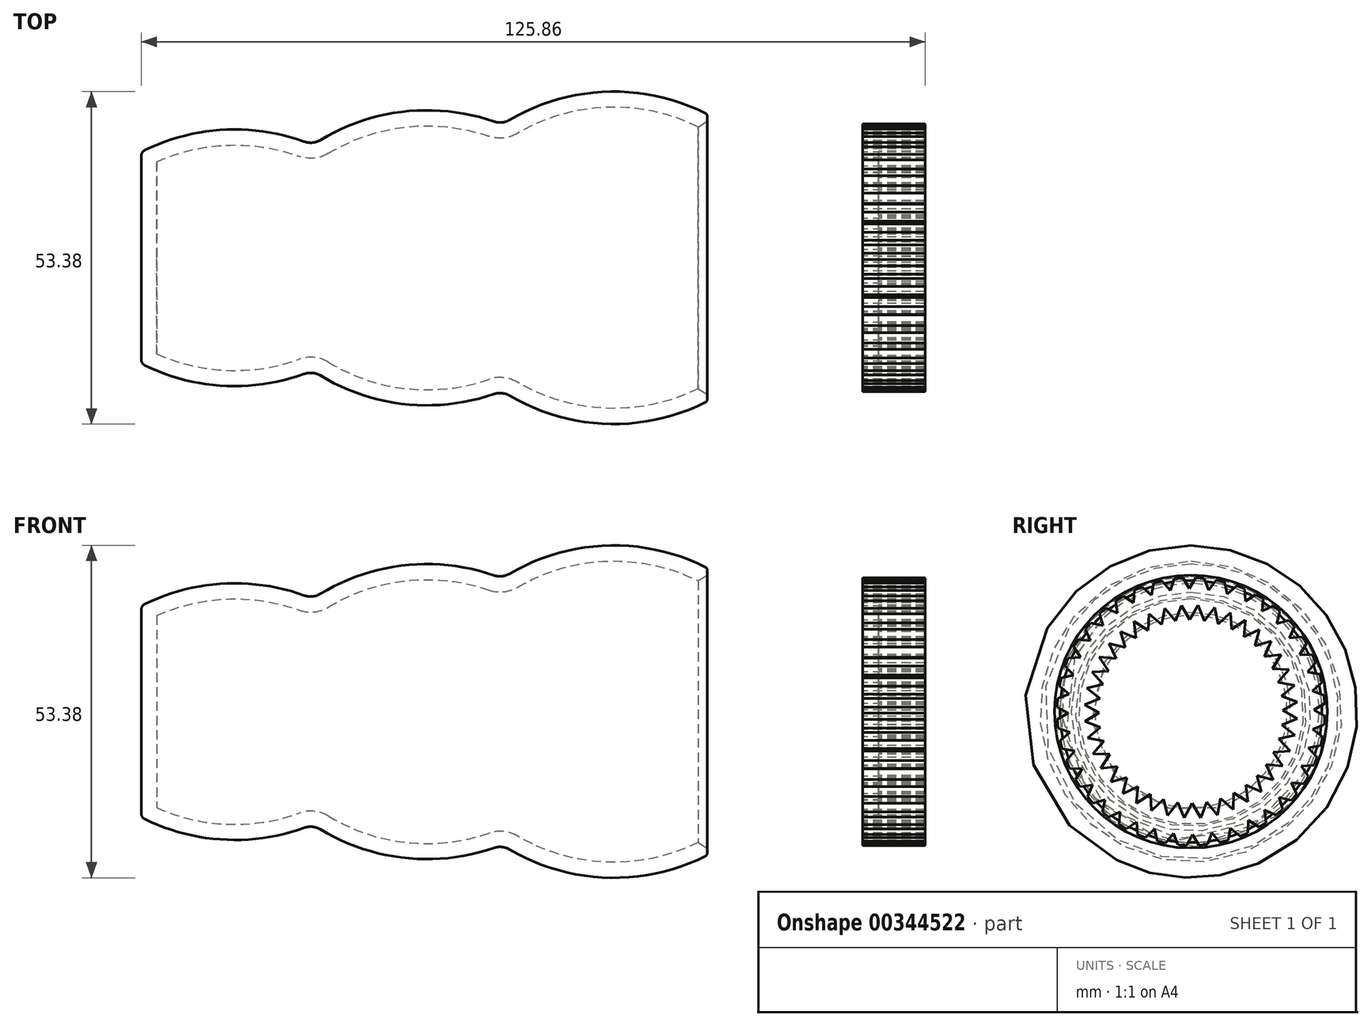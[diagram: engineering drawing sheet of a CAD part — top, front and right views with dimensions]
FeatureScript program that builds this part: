
annotation { "Feature Type Name" : "Feature", "Feature Type Description" : "" }
export const myFeature = defineFeature(function(context is Context, id is Id, definition is map)
    precondition{}
    {
        {
            var Q0;
            Q0=qCreatedBy(makeId("Front.planeOp"),FACE);
            var sketch = newSketch(context, id + "F0", { "sketchPlane" : qUnion([Q0])});
            skLineSegment(sketch, "E0.bottom", {"start": v(0, 0) * mm, "end": v(30, 0) * mm});
            skLineSegment(sketch, "E0.left", {"start": v(0, 0) * mm, "end": v(0, 16.38) * mm});
            skLineSegment(sketch, "E1.bottom", {"start": v(30, 0) * mm, "end": v(60, 0) * mm});
            skLineSegment(sketch, "E2.bottom", {"start": v(60, 0) * mm, "end": v(90.86, 0) * mm});
            skLineSegment(sketch, "E2.right", {"start": v(90.86, 0) * mm, "end": v(90.86, 23.09) * mm});
            skArc(sketch, "E3", {"start": v(26.18, 18.65) * mm, "mid": v(13.23, 20.56) * mm, "end": v(0.56, 17.28) * mm});
            skArc(sketch, "E4", {"start": v(56.63, 21.89) * mm, "mid": v(42.36, 23.5) * mm, "end": v(28.75, 18.91) * mm});
            skArc(sketch, "E5", {"start": v(90.86, 23.09) * mm, "mid": v(74.87, 26.68) * mm, "end": v(59.13, 22.14) * mm});
            skPoint(sketch, "E6.visualSharp", {"position": v(27.53, 18.13) * mm});
            skArc(sketch, "E6.filletArc", {"start": v(26.18, 18.65) * mm, "mid": v(27.5, 18.5) * mm, "end": v(28.75, 18.91) * mm});
            skPoint(sketch, "E7.visualSharp", {"position": v(57.94, 21.4) * mm});
            skArc(sketch, "E7.filletArc", {"start": v(56.63, 21.89) * mm, "mid": v(57.9, 21.74) * mm, "end": v(59.13, 22.14) * mm});
            skPoint(sketch, "E8.visualSharp", {"position": v(0, 17) * mm});
            skArc(sketch, "E8.filletArc", {"start": v(0.56, 17.28) * mm, "mid": v(0.15, 16.91) * mm, "end": v(0, 16.38) * mm});
            skSolve(sketch);
        }
        {
            var Q0;
            Q0 = qSketchRegion(id + "F0", true);
            var Q1;
            Q1=sQuery(id+"F0.wireOp",EDGE,"E1.bottom");
            revolve(context, id + "F1", {"entities" : qUnion([Q0]), "axis" : qUnion([Q1]), "revolveType" : RevolveType.FULL});
        }
        {
            var Q0;
            Q0=makeQuery(id+"F1.opRevolve","SWEPT_FACE",FACE,{"disambiguationData":[OSD([sQuery(id+"F0.wireOp",EDGE,"E2.right")])]});
            shell(context, id + "F2", {"entities" : qUnion([Q0]), "thickness" : 2.5 * mm});
        }
        {
            var Q0;
            Q0=makeQuery(id+"F2.opShell","OFFSET_EDGE",EDGE,{"disambiguationData":[OSD([sQuery(id+"F0.wireOp",EDGE,"E2.right"),sQuery(id+"F0.wireOp",EDGE,"E5")])]});
            chamfer(context, id + "F3", {"entities" : qUnion([Q0]), "width" : 1 * mm, "tangentPropagation" : true});
        }
        {
            var Q0;
            Q0=makeQuery(id+"F1.opRevolve","SWEPT_EDGE",EDGE,{"disambiguationData":[OSD([sQuery(id+"F0.wireOp",EDGE,"E2.right"),sQuery(id+"F0.wireOp",EDGE,"E5")])]});
            fillet(context, id + "F4", {"entities" : qUnion([Q0]), "radius" : 0.5 * mm, "tangentPropagation" : true, "allowEdgeOverflow" : false});
        }
        {
            var Q0;
            Q0=makeQuery(id+"F1.opRevolve","SWEPT_FACE",FACE,{"disambiguationData":[OSD([sQuery(id+"F0.wireOp",EDGE,"E2.right")])]});
            cPlane(context, id + "F5", {"entities" : qUnion([Q0]), "cplaneType" : CPlaneType.OFFSET, "offset" : 25 * mm, "width" : 150 * mm, "height" : 150 * mm});
        }
        {
            var Q0;
            Q0=qCreatedBy(id+"F5.planeOp",FACE);
            var sketch = newSketch(context, id + "F6", { "sketchPlane" : qUnion([Q0])});
            skCircle(sketch, "E9", {"center": v(0, 0) * mm, "radius": 21.5 * mm});
            skLineSegment(sketch, "E10", {"start": v(7.32, 20.21) * mm, "end": v(5.85, 18.86) * mm});
            skLineSegment(sketch, "E11", {"start": v(5.85, 18.86) * mm, "end": v(5.41, 20.8) * mm});
            skLineSegment(sketch, "E12", {"start": v(5.41, 20.8) * mm, "end": v(7.32, 20.21) * mm});
            skLineSegment(sketch, "E13.1.0", {"start": v(4.07, 21.11) * mm, "end": v(2.83, 19.54) * mm});
            skLineSegment(sketch, "E13.1.1", {"start": v(2.83, 19.54) * mm, "end": v(2.1, 21.4) * mm});
            skLineSegment(sketch, "E13.1.2", {"start": v(2.1, 21.4) * mm, "end": v(4.07, 21.11) * mm});
            skLineSegment(sketch, "E13.2.0", {"start": v(0.72, 21.49) * mm, "end": v(-0.26, 19.74) * mm});
            skLineSegment(sketch, "E13.2.1", {"start": v(-0.26, 19.74) * mm, "end": v(-1.28, 21.46) * mm});
            skLineSegment(sketch, "E13.2.2", {"start": v(-1.28, 21.46) * mm, "end": v(0.72, 21.49) * mm});
            skLineSegment(sketch, "E13.3.0", {"start": v(-2.65, 21.34) * mm, "end": v(-3.34, 19.46) * mm});
            skLineSegment(sketch, "E13.3.1", {"start": v(-3.34, 19.46) * mm, "end": v(-4.62, 21) * mm});
            skLineSegment(sketch, "E13.3.2", {"start": v(-4.62, 21) * mm, "end": v(-2.65, 21.34) * mm});
            skLineSegment(sketch, "E13.4.0", {"start": v(-5.96, 20.66) * mm, "end": v(-6.35, 18.7) * mm});
            skLineSegment(sketch, "E13.4.1", {"start": v(-6.35, 18.7) * mm, "end": v(-7.85, 20.02) * mm});
            skLineSegment(sketch, "E13.4.2", {"start": v(-7.85, 20.02) * mm, "end": v(-5.96, 20.66) * mm});
            skLineSegment(sketch, "E13.5.0", {"start": v(-9.12, 19.47) * mm, "end": v(-9.2, 17.47) * mm});
            skLineSegment(sketch, "E13.5.1", {"start": v(-9.2, 17.47) * mm, "end": v(-10.89, 18.54) * mm});
            skLineSegment(sketch, "E13.5.2", {"start": v(-10.89, 18.54) * mm, "end": v(-9.12, 19.47) * mm});
            skLineSegment(sketch, "E13.6.0", {"start": v(-12.05, 17.8) * mm, "end": v(-11.81, 15.82) * mm});
            skLineSegment(sketch, "E13.6.1", {"start": v(-11.81, 15.82) * mm, "end": v(-13.65, 16.6) * mm});
            skLineSegment(sketch, "E13.6.2", {"start": v(-13.65, 16.6) * mm, "end": v(-12.05, 17.8) * mm});
            skLineSegment(sketch, "E13.7.0", {"start": v(-14.69, 15.7) * mm, "end": v(-14.14, 13.78) * mm});
            skLineSegment(sketch, "E13.7.1", {"start": v(-14.14, 13.78) * mm, "end": v(-16.08, 14.27) * mm});
            skLineSegment(sketch, "E13.7.2", {"start": v(-16.08, 14.27) * mm, "end": v(-14.69, 15.7) * mm});
            skLineSegment(sketch, "E13.8.0", {"start": v(-16.96, 13.21) * mm, "end": v(-16.12, 11.4) * mm});
            skLineSegment(sketch, "E13.8.1", {"start": v(-16.12, 11.4) * mm, "end": v(-18.12, 11.58) * mm});
            skLineSegment(sketch, "E13.8.2", {"start": v(-18.12, 11.58) * mm, "end": v(-16.96, 13.21) * mm});
            skLineSegment(sketch, "E13.9.0", {"start": v(-18.82, 10.4) * mm, "end": v(-17.7, 8.73) * mm});
            skLineSegment(sketch, "E13.9.1", {"start": v(-17.7, 8.73) * mm, "end": v(-19.7, 8.6) * mm});
            skLineSegment(sketch, "E13.9.2", {"start": v(-19.7, 8.6) * mm, "end": v(-18.82, 10.4) * mm});
            skLineSegment(sketch, "E13.10.0", {"start": v(-20.21, 7.32) * mm, "end": v(-18.86, 5.85) * mm});
            skLineSegment(sketch, "E13.10.1", {"start": v(-18.86, 5.85) * mm, "end": v(-20.8, 5.41) * mm});
            skLineSegment(sketch, "E13.10.2", {"start": v(-20.8, 5.41) * mm, "end": v(-20.21, 7.32) * mm});
            skLineSegment(sketch, "E13.11.0", {"start": v(-21.11, 4.07) * mm, "end": v(-19.54, 2.83) * mm});
            skLineSegment(sketch, "E13.11.1", {"start": v(-19.54, 2.83) * mm, "end": v(-21.4, 2.1) * mm});
            skLineSegment(sketch, "E13.11.2", {"start": v(-21.4, 2.1) * mm, "end": v(-21.11, 4.07) * mm});
            skLineSegment(sketch, "E13.12.0", {"start": v(-21.49, 0.72) * mm, "end": v(-19.74, -0.26) * mm});
            skLineSegment(sketch, "E13.12.1", {"start": v(-19.74, -0.26) * mm, "end": v(-21.46, -1.28) * mm});
            skLineSegment(sketch, "E13.12.2", {"start": v(-21.46, -1.28) * mm, "end": v(-21.49, 0.72) * mm});
            skLineSegment(sketch, "E13.13.0", {"start": v(-21.34, -2.65) * mm, "end": v(-19.46, -3.34) * mm});
            skLineSegment(sketch, "E13.13.1", {"start": v(-19.46, -3.34) * mm, "end": v(-21, -4.62) * mm});
            skLineSegment(sketch, "E13.13.2", {"start": v(-21, -4.62) * mm, "end": v(-21.34, -2.65) * mm});
            skLineSegment(sketch, "E13.14.0", {"start": v(-20.66, -5.96) * mm, "end": v(-18.7, -6.35) * mm});
            skLineSegment(sketch, "E13.14.1", {"start": v(-18.7, -6.35) * mm, "end": v(-20.02, -7.85) * mm});
            skLineSegment(sketch, "E13.14.2", {"start": v(-20.02, -7.85) * mm, "end": v(-20.66, -5.96) * mm});
            skLineSegment(sketch, "E13.15.0", {"start": v(-19.47, -9.12) * mm, "end": v(-17.47, -9.2) * mm});
            skLineSegment(sketch, "E13.15.1", {"start": v(-17.47, -9.2) * mm, "end": v(-18.54, -10.89) * mm});
            skLineSegment(sketch, "E13.15.2", {"start": v(-18.54, -10.89) * mm, "end": v(-19.47, -9.12) * mm});
            skLineSegment(sketch, "E13.16.0", {"start": v(-17.8, -12.05) * mm, "end": v(-15.82, -11.81) * mm});
            skLineSegment(sketch, "E13.16.1", {"start": v(-15.82, -11.81) * mm, "end": v(-16.6, -13.65) * mm});
            skLineSegment(sketch, "E13.16.2", {"start": v(-16.6, -13.65) * mm, "end": v(-17.8, -12.05) * mm});
            skLineSegment(sketch, "E13.17.0", {"start": v(-15.7, -14.69) * mm, "end": v(-13.78, -14.14) * mm});
            skLineSegment(sketch, "E13.17.1", {"start": v(-13.78, -14.14) * mm, "end": v(-14.27, -16.08) * mm});
            skLineSegment(sketch, "E13.17.2", {"start": v(-14.27, -16.08) * mm, "end": v(-15.7, -14.69) * mm});
            skLineSegment(sketch, "E13.18.0", {"start": v(-13.21, -16.96) * mm, "end": v(-11.4, -16.12) * mm});
            skLineSegment(sketch, "E13.18.1", {"start": v(-11.4, -16.12) * mm, "end": v(-11.58, -18.12) * mm});
            skLineSegment(sketch, "E13.18.2", {"start": v(-11.58, -18.12) * mm, "end": v(-13.21, -16.96) * mm});
            skLineSegment(sketch, "E13.19.0", {"start": v(-10.4, -18.82) * mm, "end": v(-8.73, -17.7) * mm});
            skLineSegment(sketch, "E13.19.1", {"start": v(-8.73, -17.7) * mm, "end": v(-8.6, -19.7) * mm});
            skLineSegment(sketch, "E13.19.2", {"start": v(-8.6, -19.7) * mm, "end": v(-10.4, -18.82) * mm});
            skLineSegment(sketch, "E13.20.0", {"start": v(-7.32, -20.21) * mm, "end": v(-5.85, -18.86) * mm});
            skLineSegment(sketch, "E13.20.1", {"start": v(-5.85, -18.86) * mm, "end": v(-5.41, -20.8) * mm});
            skLineSegment(sketch, "E13.20.2", {"start": v(-5.41, -20.8) * mm, "end": v(-7.32, -20.21) * mm});
            skLineSegment(sketch, "E13.21.0", {"start": v(-4.07, -21.11) * mm, "end": v(-2.83, -19.54) * mm});
            skLineSegment(sketch, "E13.21.1", {"start": v(-2.83, -19.54) * mm, "end": v(-2.1, -21.4) * mm});
            skLineSegment(sketch, "E13.21.2", {"start": v(-2.1, -21.4) * mm, "end": v(-4.07, -21.11) * mm});
            skLineSegment(sketch, "E13.22.0", {"start": v(-0.72, -21.49) * mm, "end": v(0.26, -19.74) * mm});
            skLineSegment(sketch, "E13.22.1", {"start": v(0.26, -19.74) * mm, "end": v(1.28, -21.46) * mm});
            skLineSegment(sketch, "E13.22.2", {"start": v(1.28, -21.46) * mm, "end": v(-0.72, -21.49) * mm});
            skLineSegment(sketch, "E13.23.0", {"start": v(2.65, -21.34) * mm, "end": v(3.34, -19.46) * mm});
            skLineSegment(sketch, "E13.23.1", {"start": v(3.34, -19.46) * mm, "end": v(4.62, -21) * mm});
            skLineSegment(sketch, "E13.23.2", {"start": v(4.62, -21) * mm, "end": v(2.65, -21.34) * mm});
            skLineSegment(sketch, "E13.24.0", {"start": v(5.96, -20.66) * mm, "end": v(6.35, -18.7) * mm});
            skLineSegment(sketch, "E13.24.1", {"start": v(6.35, -18.7) * mm, "end": v(7.85, -20.02) * mm});
            skLineSegment(sketch, "E13.24.2", {"start": v(7.85, -20.02) * mm, "end": v(5.96, -20.66) * mm});
            skLineSegment(sketch, "E13.25.0", {"start": v(9.12, -19.47) * mm, "end": v(9.2, -17.47) * mm});
            skLineSegment(sketch, "E13.25.1", {"start": v(9.2, -17.47) * mm, "end": v(10.89, -18.54) * mm});
            skLineSegment(sketch, "E13.25.2", {"start": v(10.89, -18.54) * mm, "end": v(9.12, -19.47) * mm});
            skLineSegment(sketch, "E13.26.0", {"start": v(12.05, -17.8) * mm, "end": v(11.81, -15.82) * mm});
            skLineSegment(sketch, "E13.26.1", {"start": v(11.81, -15.82) * mm, "end": v(13.65, -16.6) * mm});
            skLineSegment(sketch, "E13.26.2", {"start": v(13.65, -16.6) * mm, "end": v(12.05, -17.8) * mm});
            skLineSegment(sketch, "E13.27.0", {"start": v(14.69, -15.7) * mm, "end": v(14.14, -13.78) * mm});
            skLineSegment(sketch, "E13.27.1", {"start": v(14.14, -13.78) * mm, "end": v(16.08, -14.27) * mm});
            skLineSegment(sketch, "E13.27.2", {"start": v(16.08, -14.27) * mm, "end": v(14.69, -15.7) * mm});
            skLineSegment(sketch, "E13.28.0", {"start": v(16.96, -13.21) * mm, "end": v(16.12, -11.4) * mm});
            skLineSegment(sketch, "E13.28.1", {"start": v(16.12, -11.4) * mm, "end": v(18.12, -11.58) * mm});
            skLineSegment(sketch, "E13.28.2", {"start": v(18.12, -11.58) * mm, "end": v(16.96, -13.21) * mm});
            skLineSegment(sketch, "E13.29.0", {"start": v(18.82, -10.4) * mm, "end": v(17.7, -8.73) * mm});
            skLineSegment(sketch, "E13.29.1", {"start": v(17.7, -8.73) * mm, "end": v(19.7, -8.6) * mm});
            skLineSegment(sketch, "E13.29.2", {"start": v(19.7, -8.6) * mm, "end": v(18.82, -10.4) * mm});
            skLineSegment(sketch, "E13.30.0", {"start": v(20.21, -7.32) * mm, "end": v(18.86, -5.85) * mm});
            skLineSegment(sketch, "E13.30.1", {"start": v(18.86, -5.85) * mm, "end": v(20.8, -5.41) * mm});
            skLineSegment(sketch, "E13.30.2", {"start": v(20.8, -5.41) * mm, "end": v(20.21, -7.32) * mm});
            skLineSegment(sketch, "E13.31.0", {"start": v(21.11, -4.07) * mm, "end": v(19.54, -2.83) * mm});
            skLineSegment(sketch, "E13.31.1", {"start": v(19.54, -2.83) * mm, "end": v(21.4, -2.1) * mm});
            skLineSegment(sketch, "E13.31.2", {"start": v(21.4, -2.1) * mm, "end": v(21.11, -4.07) * mm});
            skLineSegment(sketch, "E13.32.0", {"start": v(21.49, -0.72) * mm, "end": v(19.74, 0.26) * mm});
            skLineSegment(sketch, "E13.32.1", {"start": v(19.74, 0.26) * mm, "end": v(21.46, 1.28) * mm});
            skLineSegment(sketch, "E13.32.2", {"start": v(21.46, 1.28) * mm, "end": v(21.49, -0.72) * mm});
            skLineSegment(sketch, "E13.33.0", {"start": v(21.34, 2.65) * mm, "end": v(19.46, 3.34) * mm});
            skLineSegment(sketch, "E13.33.1", {"start": v(19.46, 3.34) * mm, "end": v(21, 4.62) * mm});
            skLineSegment(sketch, "E13.33.2", {"start": v(21, 4.62) * mm, "end": v(21.34, 2.65) * mm});
            skLineSegment(sketch, "E13.34.0", {"start": v(20.66, 5.96) * mm, "end": v(18.7, 6.35) * mm});
            skLineSegment(sketch, "E13.34.1", {"start": v(18.7, 6.35) * mm, "end": v(20.02, 7.85) * mm});
            skLineSegment(sketch, "E13.34.2", {"start": v(20.02, 7.85) * mm, "end": v(20.66, 5.96) * mm});
            skLineSegment(sketch, "E13.35.0", {"start": v(19.47, 9.12) * mm, "end": v(17.47, 9.2) * mm});
            skLineSegment(sketch, "E13.35.1", {"start": v(17.47, 9.2) * mm, "end": v(18.54, 10.89) * mm});
            skLineSegment(sketch, "E13.35.2", {"start": v(18.54, 10.89) * mm, "end": v(19.47, 9.12) * mm});
            skLineSegment(sketch, "E13.36.0", {"start": v(17.8, 12.05) * mm, "end": v(15.82, 11.81) * mm});
            skLineSegment(sketch, "E13.36.1", {"start": v(15.82, 11.81) * mm, "end": v(16.6, 13.65) * mm});
            skLineSegment(sketch, "E13.36.2", {"start": v(16.6, 13.65) * mm, "end": v(17.8, 12.05) * mm});
            skLineSegment(sketch, "E13.37.0", {"start": v(15.7, 14.69) * mm, "end": v(13.78, 14.14) * mm});
            skLineSegment(sketch, "E13.37.1", {"start": v(13.78, 14.14) * mm, "end": v(14.27, 16.08) * mm});
            skLineSegment(sketch, "E13.37.2", {"start": v(14.27, 16.08) * mm, "end": v(15.7, 14.69) * mm});
            skLineSegment(sketch, "E13.38.0", {"start": v(13.21, 16.96) * mm, "end": v(11.4, 16.12) * mm});
            skLineSegment(sketch, "E13.38.1", {"start": v(11.4, 16.12) * mm, "end": v(11.58, 18.12) * mm});
            skLineSegment(sketch, "E13.38.2", {"start": v(11.58, 18.12) * mm, "end": v(13.21, 16.96) * mm});
            skLineSegment(sketch, "E13.39.0", {"start": v(10.4, 18.82) * mm, "end": v(8.73, 17.7) * mm});
            skLineSegment(sketch, "E13.39.1", {"start": v(8.73, 17.7) * mm, "end": v(8.6, 19.7) * mm});
            skLineSegment(sketch, "E13.39.2", {"start": v(8.6, 19.7) * mm, "end": v(10.4, 18.82) * mm});
            skSolve(sketch);
        }
        {
            var Q0;
            {var subQ82=sQuery(id+"F6.wireOp",EDGE,"E10");Q0=makeQuery(id+"F6.imprint","IMPRINT",FACE,{"disambiguationData":[TD([[makeQuery(id+"F6.imprint","IMPRINT",EDGE,{"derivedFrom":subQ82}),1.0]])]});}
            extrude(context, id + "F7", {"entities" : qUnion([Q0]), "depth" : 10 * mm});
        }
        {
            var Q0;
            Q0=makeQuery(id+"F7.opExtrude","CAP_FACE",FACE,{"disambiguationData":[OSD([sQuery(id+"F6.wireOp",EDGE,"E9")])],"isStart":false});
            shell(context, id + "F8", {"entities" : qUnion([Q0]), "thickness" : 2.5 * mm});
        }
    });
